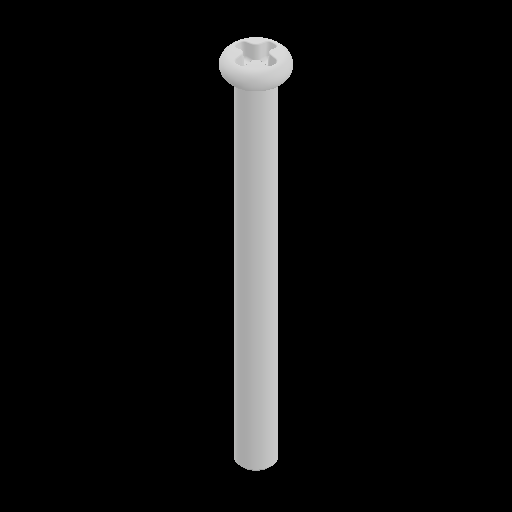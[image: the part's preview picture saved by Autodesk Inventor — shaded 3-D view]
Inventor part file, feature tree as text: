
AUTODESK INVENTOR PART (.ipt)
format: ipt  version: 2023 (Build 270158000, 158)  size: 237,056 bytes
history: native  units: mm
features: fillet x1
ambient origin geometry x8: Origin, YZ Plane, XZ Plane, XY Plane, X Axis, Y Axis, Z Axis, Center Point
bodies: Solid1 (feature_tree)
feature tree (1):
  fillet  "Fillet4"  [1 undecoded]
note: 1 required parameter value undecoded (feature->parameter linkage not recoverable at this tier; creation-order binding heuristic only, values carry confidence <= 0.55)
